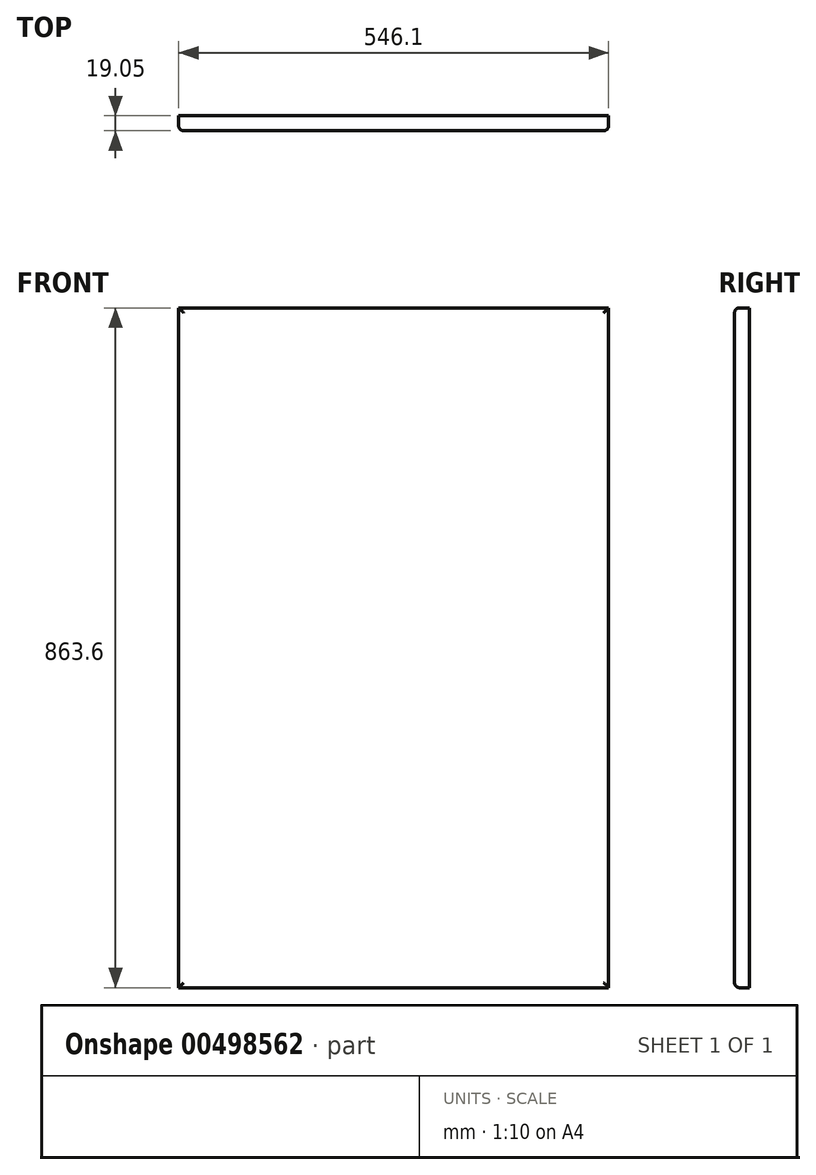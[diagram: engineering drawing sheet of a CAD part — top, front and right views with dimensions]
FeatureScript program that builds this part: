
annotation { "Feature Type Name" : "Feature", "Feature Type Description" : "" }
export const myFeature = defineFeature(function(context is Context, id is Id, definition is map)
    precondition{}
    {
        {
            var Q0;
            Q0=qCreatedBy(makeId("Front.planeOp"),FACE);
            var sketch = newSketch(context, id + "F0", { "sketchPlane" : qUnion([Q0])});
            skLineSegment(sketch, "E0.bottom", {"start": v(0, 0) * mm, "end": v(546.1, 0) * mm});
            skLineSegment(sketch, "E0.top", {"start": v(0, 863.6) * mm, "end": v(546.1, 863.6) * mm});
            skLineSegment(sketch, "E0.left", {"start": v(0, 0) * mm, "end": v(0, 863.6) * mm});
            skLineSegment(sketch, "E0.right", {"start": v(546.1, 0) * mm, "end": v(546.1, 863.6) * mm});
            skSolve(sketch);
        }
        {
            var Q0;
            Q0 = qSketchRegion(id + "F0", true);
            extrude(context, id + "F1", {"entities" : qUnion([Q0]), "depth" : 19.05 * mm, "offsetDistance" : 25.4 * mm});
        }
        {
            var Q0;
            Q0=makeQuery(id+"F1.opExtrude","CAP_EDGE",EDGE,{"disambiguationData":[OSD([sQuery(id+"F0.wireOp",EDGE,"E0.left")])],"isStart":false});
            var Q1;
            Q1=makeQuery(id+"F1.opExtrude","CAP_EDGE",EDGE,{"disambiguationData":[OSD([sQuery(id+"F0.wireOp",EDGE,"E0.bottom")])],"isStart":false});
            var Q2;
            Q2=makeQuery(id+"F1.opExtrude","CAP_EDGE",EDGE,{"disambiguationData":[OSD([sQuery(id+"F0.wireOp",EDGE,"E0.right")])],"isStart":false});
            var Q3;
            Q3=makeQuery(id+"F1.opExtrude","CAP_EDGE",EDGE,{"disambiguationData":[OSD([sQuery(id+"F0.wireOp",EDGE,"E0.top")])],"isStart":false});
            fillet(context, id + "F2", {"entities" : qUnion([Q0, Q1, Q2, Q3]), "radius" : 6.35 * mm, "tangentPropagation" : true, "allowEdgeOverflow" : false});
        }
    });
